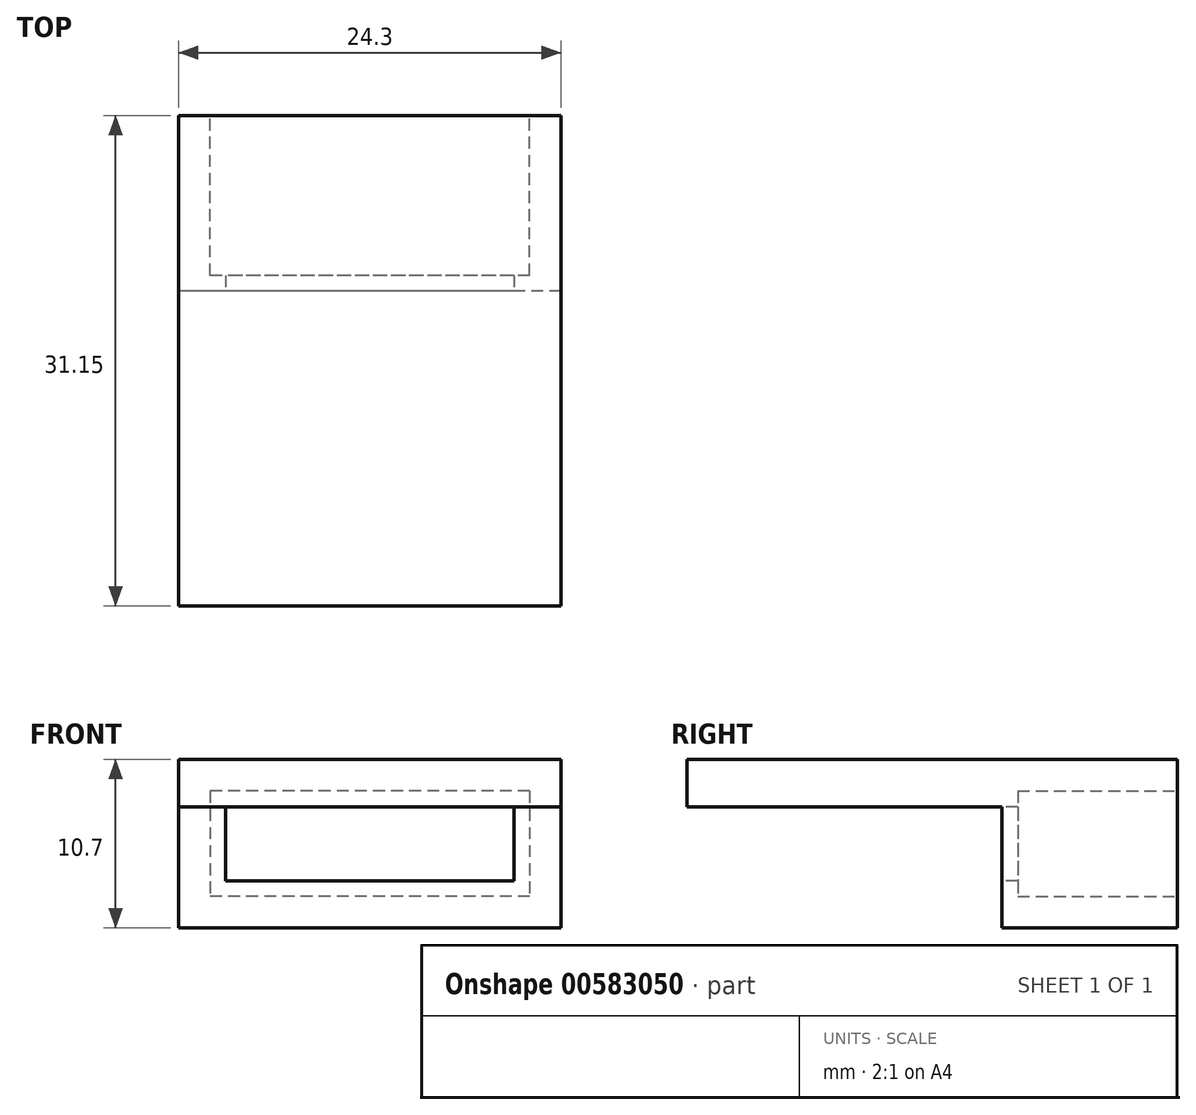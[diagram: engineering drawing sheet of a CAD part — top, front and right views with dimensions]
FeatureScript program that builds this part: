
annotation { "Feature Type Name" : "Feature", "Feature Type Description" : "" }
export const myFeature = defineFeature(function(context is Context, id is Id, definition is map)
    precondition{}
    {
        {
            var Q0;
            Q0=qCreatedBy(makeId("Front.planeOp"),FACE);
            var sketch = newSketch(context, id + "F0", { "sketchPlane" : qUnion([Q0])});
            skLineSegment(sketch, "E0.bottom", {"start": v(10.15, 3.35) * mm, "end": v(-10.15, 3.35) * mm});
            skLineSegment(sketch, "E0.top", {"start": v(10.15, -3.35) * mm, "end": v(-10.15, -3.35) * mm});
            skLineSegment(sketch, "E0.left", {"start": v(10.15, 3.35) * mm, "end": v(10.15, -3.35) * mm});
            skLineSegment(sketch, "E0.right", {"start": v(-10.15, 3.35) * mm, "end": v(-10.15, -3.35) * mm});
            skPoint(sketch, "E0.middle", {"position": v(0, 0) * mm});
            skLineSegment(sketch, "E1.0", {"start": v(12.15, 5.35) * mm, "end": v(-12.15, 5.35) * mm});
            skLineSegment(sketch, "E1.1", {"start": v(12.15, 5.35) * mm, "end": v(12.15, -5.35) * mm});
            skLineSegment(sketch, "E1.2", {"start": v(12.15, -5.35) * mm, "end": v(-12.15, -5.35) * mm});
            skLineSegment(sketch, "E1.3", {"start": v(-12.15, 5.35) * mm, "end": v(-12.15, -5.35) * mm});
            skSolve(sketch);
        }
        {
            var Q0;
            Q0 = qSketchRegion(id + "F0", true);
            extrude(context, id + "F1", {"entities" : qUnion([Q0]), "depth" : 11.15 * mm, "offsetDistance" : 25 * mm});
        }
        {
            var Q0;
            Q0=makeQuery(id+"F1.opExtrude","CAP_FACE",FACE,{"disambiguationData":[OSD([sQuery(id+"F0.wireOp",EDGE,"E0.bottom"),sQuery(id+"F0.wireOp",EDGE,"E0.top"),sQuery(id+"F0.wireOp",EDGE,"E0.left"),sQuery(id+"F0.wireOp",EDGE,"E0.right"),sQuery(id+"F0.wireOp",EDGE,"E1.0"),sQuery(id+"F0.wireOp",EDGE,"E1.1"),sQuery(id+"F0.wireOp",EDGE,"E1.2"),sQuery(id+"F0.wireOp",EDGE,"E1.3")])],"isStart":false});
            var sketch = newSketch(context, id + "F2", { "sketchPlane" : qUnion([Q0])});
            skLineSegment(sketch, "E2.0", {"start": v(9.15, 2.35) * mm, "end": v(-9.15, 2.35) * mm});
            skLineSegment(sketch, "E2.1", {"start": v(9.15, 2.35) * mm, "end": v(9.15, -2.35) * mm});
            skLineSegment(sketch, "E2.2", {"start": v(9.15, -2.35) * mm, "end": v(-9.15, -2.35) * mm});
            skLineSegment(sketch, "E2.3", {"start": v(-9.15, 2.35) * mm, "end": v(-9.15, -2.35) * mm});
            skLineSegment(sketch, "E3.0", {"start": v(10.15, 3.35) * mm, "end": v(-10.15, 3.35) * mm});
            skLineSegment(sketch, "E4.0", {"start": v(-10.15, 3.35) * mm, "end": v(-10.15, -3.35) * mm});
            skLineSegment(sketch, "E5.0", {"start": v(10.15, -3.35) * mm, "end": v(-10.15, -3.35) * mm});
            skLineSegment(sketch, "E6.0", {"start": v(10.15, 3.35) * mm, "end": v(10.15, -3.35) * mm});
            skSolve(sketch);
        }
        {
            var Q0;
            Q0 = qSketchRegion(id + "F2", true);
            extrude(context, id + "F3", {"entities" : qUnion([Q0]), "operationType" : NewBodyOperationType.ADD, "oppositeDirection" : true, "depth" : 1 * mm, "offsetDistance" : 25 * mm});
        }
        {
            var Q0;
            Q0=makeQuery(id+"F3.boolean.opBoolean","MERGE",FACE,{"derivedFrom":[makeQuery(id+"F1.opExtrude","CAP_FACE",FACE,{"disambiguationData":[OSD([sQuery(id+"F0.wireOp",EDGE,"E0.bottom"),sQuery(id+"F0.wireOp",EDGE,"E0.top"),sQuery(id+"F0.wireOp",EDGE,"E0.left"),sQuery(id+"F0.wireOp",EDGE,"E0.right"),sQuery(id+"F0.wireOp",EDGE,"E1.0"),sQuery(id+"F0.wireOp",EDGE,"E1.1"),sQuery(id+"F0.wireOp",EDGE,"E1.2"),sQuery(id+"F0.wireOp",EDGE,"E1.3")])],"isStart":false}),makeQuery(id+"F3.opExtrude","CAP_FACE",FACE,{"disambiguationData":[OSD([sQuery(id+"F2.wireOp",EDGE,"E2.0"),sQuery(id+"F2.wireOp",EDGE,"E2.1"),sQuery(id+"F2.wireOp",EDGE,"E2.2"),sQuery(id+"F2.wireOp",EDGE,"E2.3"),sQuery(id+"F2.wireOp",EDGE,"E3.0"),sQuery(id+"F2.wireOp",EDGE,"E4.0"),sQuery(id+"F2.wireOp",EDGE,"E5.0"),sQuery(id+"F2.wireOp",EDGE,"E6.0")])],"isStart":true})]});
            var sketch = newSketch(context, id + "F4", { "sketchPlane" : qUnion([Q0])});
            skLineSegment(sketch, "E7.0", {"start": v(12.15, 5.35) * mm, "end": v(-12.15, 5.35) * mm});
            skLineSegment(sketch, "E8.0", {"start": v(9.15, 2.35) * mm, "end": v(-9.15, 2.35) * mm});
            skLineSegment(sketch, "E9.0", {"start": v(12.15, 5.35) * mm, "end": v(12.15, 2.35) * mm});
            skLineSegment(sketch, "E10.0", {"start": v(-12.15, 5.35) * mm, "end": v(-12.15, 2.35) * mm});
            skLineSegment(sketch, "E11", {"start": v(9.15, 2.35) * mm, "end": v(12.15, 2.35) * mm});
            skLineSegment(sketch, "E12", {"start": v(-9.15, 2.35) * mm, "end": v(-12.15, 2.35) * mm});
            skPoint(sketch, "E13.orphan", {"position": v(12.15, -5.35) * mm});
            skPoint(sketch, "E14.orphan", {"position": v(-12.15, -5.35) * mm});
            skSolve(sketch);
        }
        {
            var Q0;
            Q0 = qSketchRegion(id + "F4", true);
            extrude(context, id + "F5", {"entities" : qUnion([Q0]), "operationType" : NewBodyOperationType.ADD, "depth" : 20 * mm, "offsetDistance" : 25 * mm});
        }
    });
